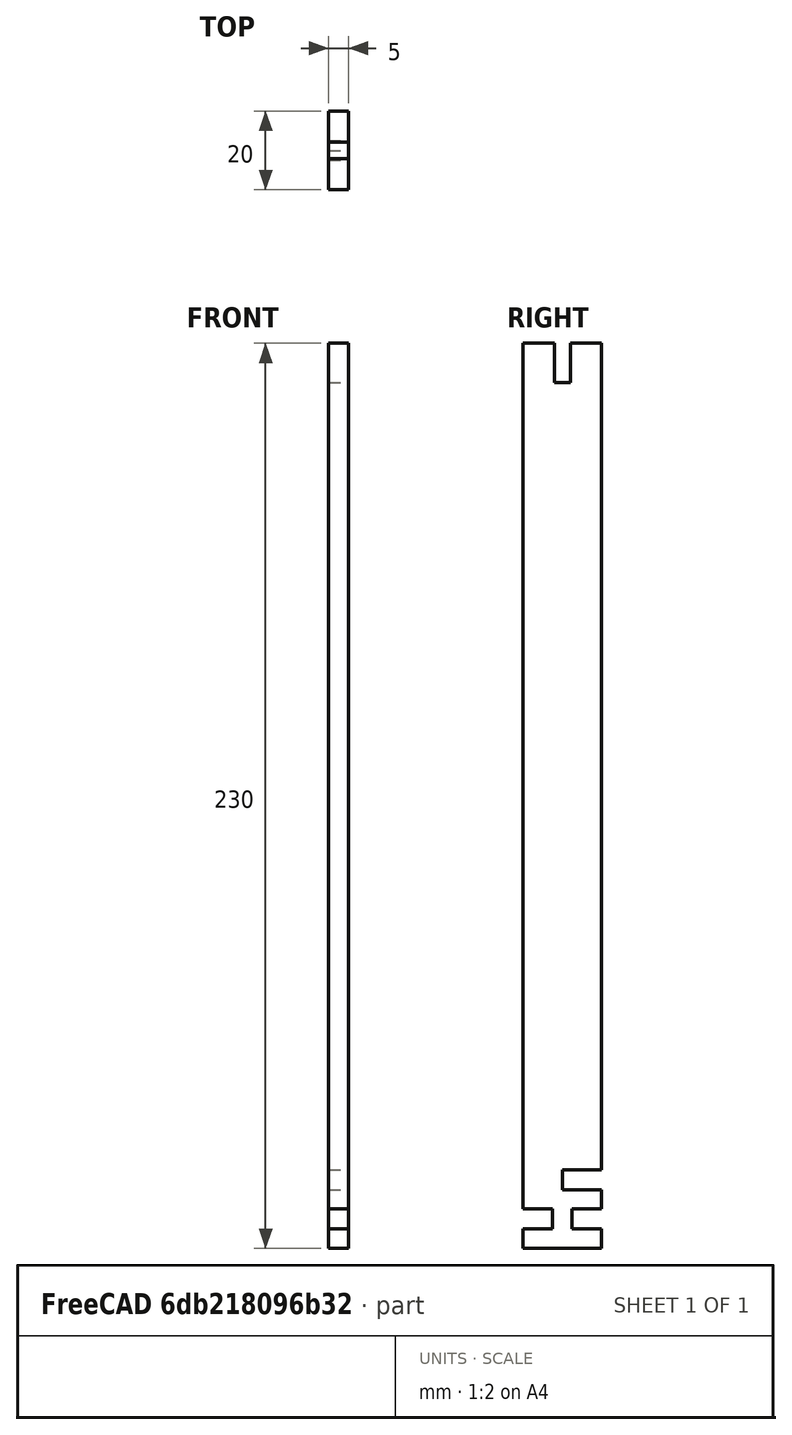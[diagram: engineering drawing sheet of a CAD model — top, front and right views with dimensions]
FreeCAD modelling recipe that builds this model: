
FCSTD DOCUMENT  (FreeCAD 1.0R39319 (Git))
Label: Z Axis Leg
License: All rights reserved
LicenseURL: https://en.wikipedia.org/wiki/All_rights_reserved
objects: PartDesign::CoordinateSystem×3, Sketcher::SketchObject×1, PartDesign::Pad×1, PartDesign::Body×1, App::Part×1
note: 9 computed .brp shape members not serialized (recipe doc carries the construction recipe); baked Part::Feature solids carry a one-line shape summary decoded from their .brp

FEATURE [Sketcher::SketchObject] Sketch
  ArcFitTolerance = 1e-06
  AttachmentSupport = -> [YZ_Plane001]
  FullyConstrained = true
  MakeInternals = false
  MapMode = 5
  Placement = pos=(0,0,0) rot=(0.57735,0.57735,0.57735;2.0944rad)
  sketch-geometry (25):
    g0: LineSegment StartX=10 StartY=0 StartZ=0 EndX=10 EndY=4.95 EndZ=0
    g1: LineSegment StartX=10 StartY=230 StartZ=0 EndX=2.05 EndY=230 EndZ=0
    g2: LineSegment StartX=-10 StartY=230 StartZ=0 EndX=-10 EndY=10.05 EndZ=0
    g3: LineSegment StartX=-10 StartY=0 StartZ=0 EndX=10 EndY=0 EndZ=0
    g4: LineSegment StartX=-2.05 StartY=230 StartZ=0 EndX=-2.05 EndY=220 EndZ=0
    g5: LineSegment StartX=-2.05 StartY=220 StartZ=0 EndX=2.05 EndY=220 EndZ=0
    g6: LineSegment StartX=2.05 StartY=220 StartZ=0 EndX=2.05 EndY=230 EndZ=0
    g7: LineSegment StartX=-2.05 StartY=230 StartZ=0 EndX=-10 EndY=230 EndZ=0
    g8: LineSegment StartX=10 StartY=10.05 StartZ=0 EndX=2.5 EndY=10.05 EndZ=0
    g9: LineSegment StartX=2.5 StartY=10.05 StartZ=0 EndX=2.5 EndY=4.95 EndZ=0
    g10: LineSegment StartX=2.5 StartY=4.95 StartZ=0 EndX=10 EndY=4.95 EndZ=0
    g11: LineSegment StartX=-10 StartY=4.95 StartZ=0 EndX=-2.5 EndY=4.95 EndZ=0
    g12: LineSegment StartX=-2.5 StartY=4.95 StartZ=0 EndX=-2.5 EndY=10.05 EndZ=0
    g13: LineSegment StartX=-2.5 StartY=10.05 StartZ=0 EndX=-10 EndY=10.05 EndZ=0
    g14: LineSegment StartX=10 StartY=20.05 StartZ=0 EndX=0 EndY=20.05 EndZ=0
    g15: LineSegment StartX=0 StartY=20.05 StartZ=0 EndX=0 EndY=14.95 EndZ=0
    g16: LineSegment StartX=0 StartY=14.95 StartZ=0 EndX=10 EndY=14.95 EndZ=0
    g17: LineSegment StartX=10 StartY=20.05 StartZ=0 EndX=10 EndY=230 EndZ=0
    g18: LineSegment StartX=10 StartY=10.05 StartZ=0 EndX=10 EndY=14.95 EndZ=0
    g19: LineSegment StartX=-10 StartY=4.95 StartZ=0 EndX=-10 EndY=0 EndZ=0
    g20: GeomPoint [constr] X=0 Y=17.5 Z=0
    g21: GeomPoint [constr] X=2.5 Y=7.5 Z=0
    g22: GeomPoint [constr] X=-2.5 Y=7.5 Z=0
    g23: GeomPoint [constr] X=-1e-16 Y=220 Z=0
    g24: LineSegment [constr] StartX=-2.5 StartY=7.5 StartZ=0 EndX=2.5 EndY=7.5 EndZ=0
  constraints (69):
    c: Coincident(g17,g1)
    c: Coincident(g7,g2)
    c: Coincident(g19,g3)
    c: Coincident(g3,g0)
    c: Vertical(g0)
    c: Vertical(g2)
    c: Horizontal(g1)
    c: Horizontal(g3)
    c: Coincident(g4,g5)
    c: Coincident(g5,g6)
    c: Vertical(g4)
    c: Vertical(g6)
    c: Horizontal(g5)
    c: PointOnObject(g4,g7)
    c: PointOnObject(g7,g4)
    c: Coincident(g8,g9)
    c: Coincident(g9,g10)
    c: Horizontal(g8)
    c: Horizontal(g10)
    c: Vertical(g9)
    c: PointOnObject(g8,g18)
    c: Coincident(g11,g12)
    c: Coincident(g12,g13)
    c: Vertical(g12)
    c: Horizontal(g11)
    c: Horizontal(g13)
    c: Coincident(g14,g15)
    c: Coincident(g15,g16)
    c: Horizontal(g14)
    c: Horizontal(g16)
    c: Vertical(g15)
    c: PointOnObject(g14,g17)
    c: PointOnObject(g17,g14)
    c: PointOnObject(g18,g8)
    c: Symmetric(g15,g15,g20)
    c: Symmetric(g9,g9,g21)
    c: Symmetric(g12,g12,g22)
    c: Symmetric(g5,g5,g23)
    c: Coincident(g24,g22)
    c: Coincident(g24,g21)
    c: Horizontal(g24)
    c: Coincident(g2,g13)
    c: Coincident(g19,g11)
    c: DistanceY(g15,g15) = 5.1
    c: DistanceY(g9,g9) = 5.1
    c: PointOnObject(g8,g13)
    c: Distance(g3,g24) = 7.5
    c: DistanceX(g3,g3) = 20
    c: Vertical(g19)
    c: PointOnObject(g11,g2)
    c: PointOnObject(g8,g0)
    c: Coincident(g16,g18)
    c: Vertical(g18)
    c: Vertical(g17)
    c: PointOnObject(g14,g18)
    c: Coincident(g10,g0)
    c: Distance(g0,g9) = 7.5
    c: Distance(g12,g19) = 7.5
    c: DistanceX(g14,g14) = 10
    c: DistanceY(g21,g20) = 10
    c: Distance(g6,g4) = 4.1
    c: Coincident(g6,g1)
    c: Horizontal(g7)
    c: PointOnObject(g1,g7)
    c: DistanceY(g6,g6) = 10
    c: Distance(g7,g3) = 230
    c: Distance(g23,g17) = 10
    c: PointOnObject(g20,g-2)
    c: PointOnObject(g3,g-1)
FEATURE [PartDesign::Pad] Pad
  Direction = (1,0,0)
  Length = 5
  Length2 = 10
  Midplane = true
  Placement = pos=(0,0,0) rot=(1,1,1;2.0944rad)
  Profile = -> Sketch
  ReferenceAxis = -> Sketch [N_Axis]
  Refine = true
  Suppressed = false
  Type = 0
FEATURE [PartDesign::Body] Body  label="Z Axis Leg001"
  AllowCompound = false
  Group = -> [Sketch,Pad]
  Origin = -> Origin001
  Tip = -> Pad
FEATURE [PartDesign::CoordinateSystem] LCS_1
  AttacherType = Attacher::AttachEngine3D
  AttachmentOffset = pos=(-2.5,0,7.5) rot=(0,0,1;0rad)
  AttachmentSupport = -> [XY_Plane001]
  MapMode = 2
  Placement = pos=(-2.5,0,7.5) rot=(0,0,1;0rad)
FEATURE [PartDesign::CoordinateSystem] LCS_2
  AttacherType = Attacher::AttachEngine3D
  AttachmentOffset = pos=(0,0,17.5) rot=(0,0,1;0rad)
  AttachmentSupport = -> [XY_Plane001]
  MapMode = 2
  Placement = pos=(0,0,17.5) rot=(0,0,1;0rad)
FEATURE [PartDesign::CoordinateSystem] LCS_3
  AttacherType = Attacher::AttachEngine3D
  AttachmentOffset = pos=(0,0,220) rot=(0,0,1;0rad)
  AttachmentSupport = -> [XY_Plane001]
  MapMode = 2
  Placement = pos=(0,0,220) rot=(0,0,1;0rad)
FEATURE [App::Part] Part  label="Z Axis Leg"
  Group = -> [Body,LCS_1,LCS_2,LCS_3]
  Origin = -> Origin
